# Revit family: LAMP_BAZZ REC ASYMMETRIC
name_source: partatom
category: Modelos genéricos
revit_build: Autodesk Revit 2018 (Build: 20190510_1515(x64)
units: mm (PartAtom-declared; Revit-internal decimal feet)

## family parameters
Anfitrión = Cara
Compartido = No
Corte con vacíos al cargar = No
Cota de conector redondo = Diámetro de uso
Puede alojar armadura = No
Punto de cálculo de habitación = No
Tipo de pieza = Normal

## types (8) — shared parameters
CRI = 80
Elevación por defecto = 1219 mm
Fabricante = LAMP
Finish = Anodized matte black
Gear = Electronic
Height = 84 mm  [stored 0.275591 ft]
Installation instructions = http://www.lamp.es
Insulation class = I
LED Lifetime = 50.000 L80 B10
Lamp = MID-POWER LED
Last update = 17/02/2022
Luminaire type = Outdoor -Recessed luminaire
MacAdam = <3
Manufacturer URL = http://www.lamp.es
Manufacturer country = Spain
Manufacturer name = LAMP
Power Supply = 220-240V 50/60Hz
Product URL = http://www.lamp.es
Product datasheet = http://www.lamp.es
Protection rating = IP67 / IK07
Type = MID POWER SAMSUNG

## per-type parameters (varying)
| type | Descripción | Dimensions | Efficacy | Initial color | Initial intensity | Modelo | Photometric web file | Plum | Power | Product code | Weight |
| 1981LM 3000 1M | BAZZ REC ASYM 1M 2100 WW | 1043x106x84 | 96 lm/W | 3000 K | 1981 lm | BZ1RE100LOAS830NB | Bazz rec asymmetric - base : 1981LM 3000 1M | 21 W | 19 W | BZ1RE100LOAS830NB | 5.28 kg |
| 2080LM 4000 1M | BAZZ REC ASYM 1M 2100 NW | 1043x106x84 | 101 lm/W | 4000 K | 2080 lm | BZ1RE100LOAS840NB | Bazz rec asymmetric - base : 2080LM 4000 1M | 21 W | 19 W | BZ1RE100LOAS840NB | 5.28 kg |
| 3883LM 3000 1M | BAZZ REC ASYM 1M 4200 WW | 1043x106x84 | 97 lm/W | 3000 K | 3883 lm | BZ1RE100MOAS830NB | Bazz rec asymmetric - base : 3883LM 3000 1M | 40 W | 37 W | BZ1RE100MOAS830NB | 5.43 kg |
| 4077LM 4000 1M | BAZZ REC ASYM 2M 4200 WW | 1043x106x84 | 99 lm/W | 3000 K | 3962 lm | BZ1RE200LOAS830NB | Bazz rec asymmetric - base : 4077LM 4000 1M | 40 W | 38 W | BZ1RE200LOAS830NB | 9.89 kg |
| 3962LM 3000 2M | BAZZ REC ASYM 1M 4200 NW | 1043x106x84 | 102 lm/W | 4000 K | 4077 lm | BZ1RE100MOAS840NB | Bazz rec asymmetric - base : 3962LM 3000 2M | 40 W | 37 W | BZ1RE100MOAS840NB | 5.43 kg |
| 4160LM 4000 2M | BAZZ REC ASYM 2M 4200 NW | 2036x106x84 | 104 lm/W | 4000 K | 4160 lm | BZ1RE200LOAS840NB | Bazz rec asymmetric - base : 4160LM 4000 2M | 40 W | 38 W | BZ1RE200LOAS840NB | 9.89 kg |
| 7766LM 3000 2M | BAZZ REC ASYM 2M 8100 WW | 2036x106x84 | 101 lm/W | 3000 K | 7766 lm | BZ1RE200MOAS830NB | Bazz rec asymmetric - base : 7766LM 3000 2M | 77 W | 75 W | BZ1RE200MOAS830NB | 10.04 kg |
| 8154LM 4000 2M | BAZZ REC ASYM 2M 8100 NW | 2036x106x84 | 106 lm/W | 4000 K | 8158 lm | BZ1RE200MOAS840NB | Bazz rec asymmetric - base : 8154LM 4000 2M | 77 W | 75 W | BZ1RE200MOAS840NB | 10.04 kg |

note: [stored X ft] marks values corroborated as IEEE doubles in the binary element streams (Revit-internal decimal feet)

## geometry (parser evidence)
native form markers: Blend x4
no freeform markers — native parametric forms only
